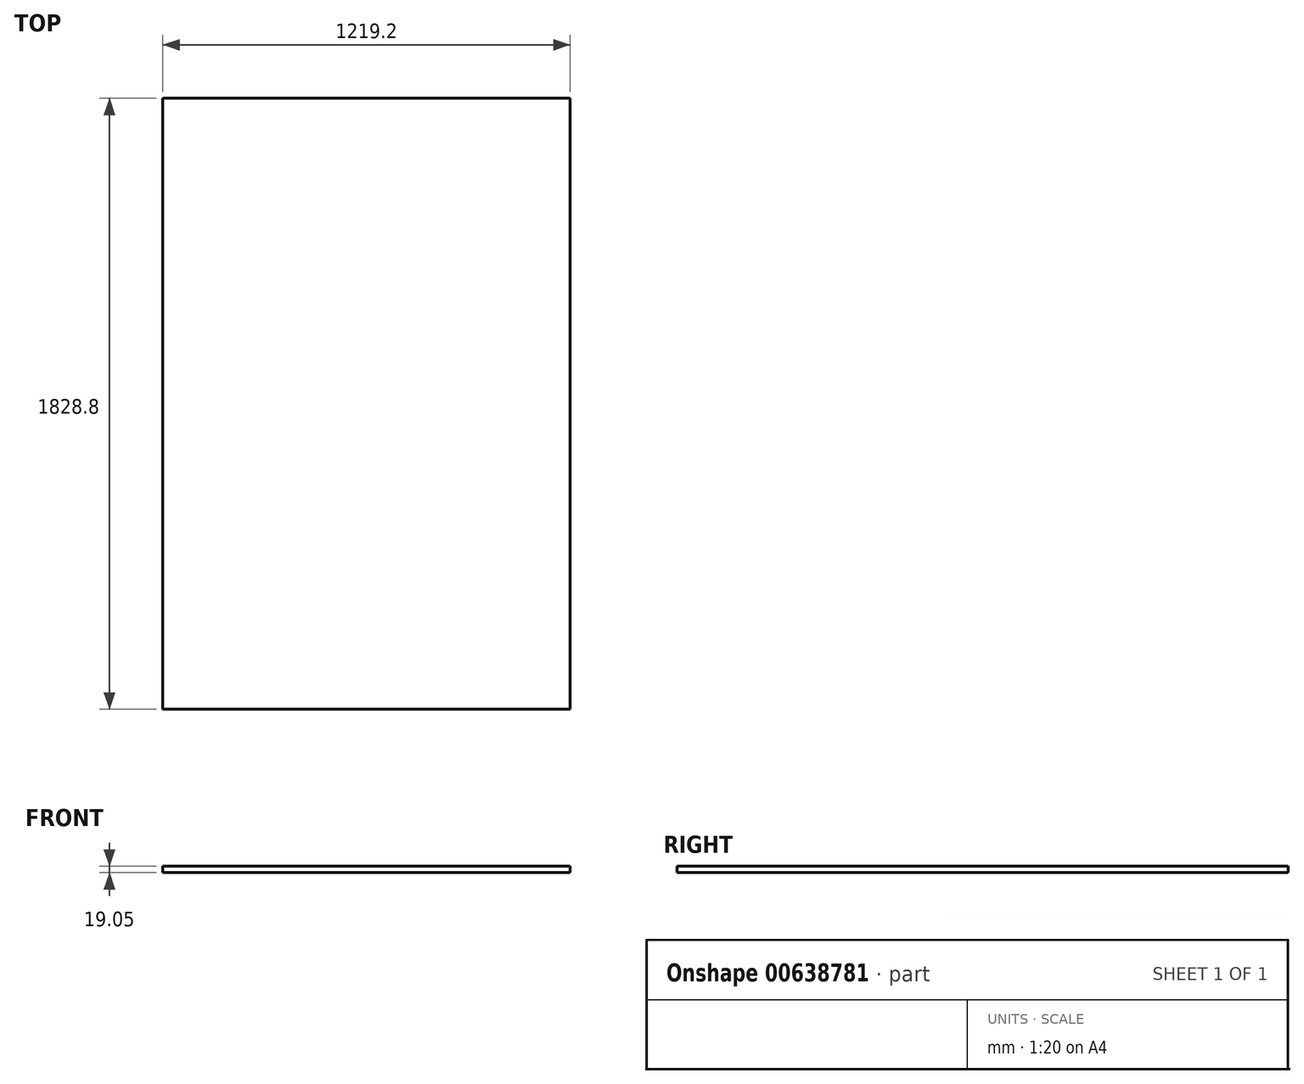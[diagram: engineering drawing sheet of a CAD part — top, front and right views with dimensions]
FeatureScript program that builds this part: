
annotation { "Feature Type Name" : "Feature", "Feature Type Description" : "" }
export const myFeature = defineFeature(function(context is Context, id is Id, definition is map)
    precondition{}
    {
        {
            var Q0;
            Q0=qCreatedBy(makeId("Top.planeOp"),FACE);
            var sketch = newSketch(context, id + "F0", { "sketchPlane" : qUnion([Q0])});
            skLineSegment(sketch, "E0.bottom", {"start": v(-609.6, 914.4) * mm, "end": v(609.6, 914.4) * mm});
            skLineSegment(sketch, "E0.top", {"start": v(-609.6, -914.4) * mm, "end": v(609.6, -914.4) * mm});
            skLineSegment(sketch, "E0.left", {"start": v(-609.6, 914.4) * mm, "end": v(-609.6, -914.4) * mm});
            skLineSegment(sketch, "E0.right", {"start": v(609.6, 914.4) * mm, "end": v(609.6, -914.4) * mm});
            skPoint(sketch, "E0.middle", {"position": v(0, 0) * mm});
            skSolve(sketch);
        }
        {
            var Q0;
            Q0=makeQuery(id+"F0.imprint","IMPRINT",FACE,{"disambiguationData":[TD([[makeQuery(id+"F0.imprint","IMPRINT",EDGE,{"derivedFrom":sQuery(id+"F0.wireOp",EDGE,"E0.bottom")}),-1.0]])]});
            extrude(context, id + "F1", {"entities" : qUnion([Q0]), "depth" : 19.05 * mm, "offsetDistance" : 25.4 * mm});
        }
    });
